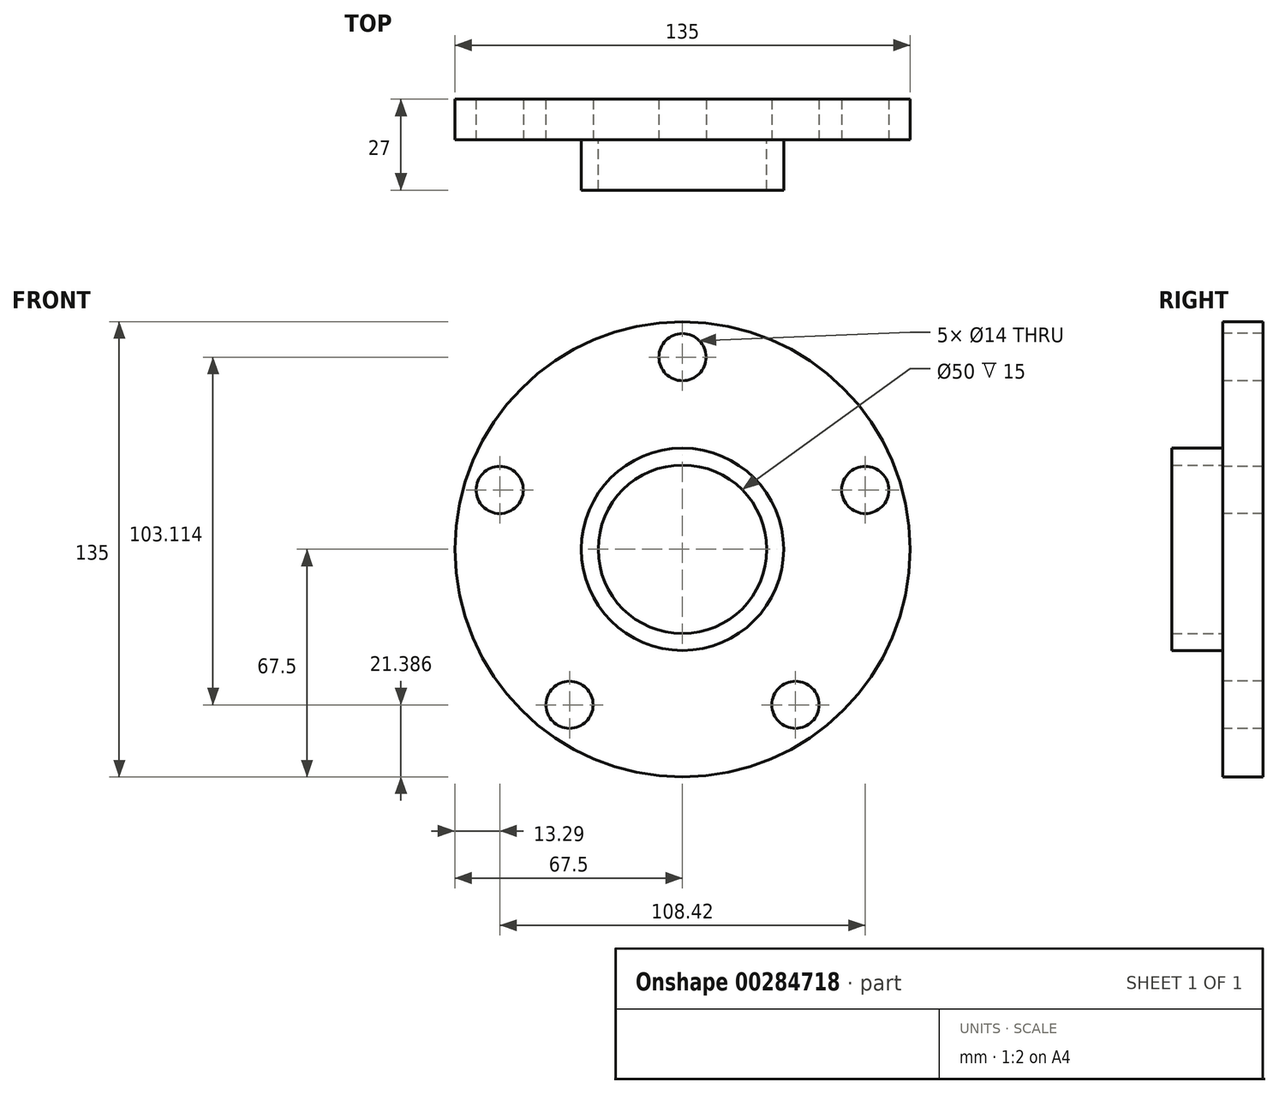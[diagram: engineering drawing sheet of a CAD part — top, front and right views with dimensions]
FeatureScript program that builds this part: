
annotation { "Feature Type Name" : "Feature", "Feature Type Description" : "" }
export const myFeature = defineFeature(function(context is Context, id is Id, definition is map)
    precondition{}
    {
        {
            var Q0;
            Q0=qCreatedBy(makeId("Front.planeOp"),FACE);
            var sketch = newSketch(context, id + "F0", { "sketchPlane" : qUnion([Q0])});
            skCircle(sketch, "E0", {"center": v(0, 0) * mm, "radius": 67.5 * mm});
            skSolve(sketch);
        }
        {
            var Q0;
            Q0=qSketchRegion(id+"F0",true);
            extrude(context, id + "F1", {"entities" : qUnion([Q0]), "depth" : 12 * mm});
        }
        {
            var Q0;
            Q0=makeQuery(id+"F1.opExtrude","CAP_FACE",FACE,{"disambiguationData":[OSD([sQuery(id+"F0.wireOp",EDGE,"E0")])],"isStart":false});
            var sketch = newSketch(context, id + "F2", { "sketchPlane" : qUnion([Q0])});
            skCircle(sketch, "E1", {"center": v(0, 0) * mm, "radius": 30 * mm});
            skCircle(sketch, "E2", {"center": v(0, 0) * mm, "radius": 25 * mm});
            skSolve(sketch);
        }
        {
            var Q0;
            Q0=qSketchRegion(id+"F2",true);
            extrude(context, id + "F3", {"entities" : qUnion([Q0]), "operationType" : NewBodyOperationType.ADD, "depth" : 15 * mm});
        }
        {
            var Q0;
            {var subQ0=sQuery(id+"F0.wireOp",EDGE,"E0");Q0=makeQuery(id+"F3.boolean.opBoolean","SPLIT",FACE,{"disambiguationData":[TD([makeQuery(id+"F1.opExtrude","SWEPT_FACE",FACE,{"disambiguationData":[OSD([subQ0])]})])],"derivedFrom":makeQuery(id+"F1.opExtrude","CAP_FACE",FACE,{"disambiguationData":[OSD([subQ0])],"isStart":false})});}
            var sketch = newSketch(context, id + "F4", { "sketchPlane" : qUnion([Q0])});
            skLineSegment(sketch, "E3", {"start": v(0, 0) * mm, "end": v(0, 57) * mm});
            skCircle(sketch, "E4", {"center": v(0, 57) * mm, "radius": 7 * mm});
            skSolve(sketch);
        }
        {
            var Q0;
            Q0=qSketchRegion(id+"F4",true);
            extrude(context, id + "F5", {"entities" : qUnion([Q0]), "operationType" : NewBodyOperationType.REMOVE, "oppositeDirection" : true, "depth" : 15 * mm});
        }
        {
            var Q0;
            Q0=makeQuery(id+"F5.boolean.opBoolean","COPY",FACE,{"derivedFrom":makeQuery(id+"F5.opExtrude","SWEPT_FACE",FACE,{"disambiguationData":[OSD([sQuery(id+"F4.wireOp",EDGE,"E4")])]})});
            var Q1;
            Q1=makeQuery(id+"F1.opExtrude","CAP_EDGE",EDGE,{"disambiguationData":[OSD([sQuery(id+"F0.wireOp",EDGE,"E0")])],"isStart":false});
            circularPattern(context, id + "F6", {"patternType" : PatternType.FACE, "faces" : qUnion([Q0]), "axis" : qUnion([Q1]), "angle" : 360 * degree, "instanceCount" : 5, "equalSpace" : true});
        }
    });
